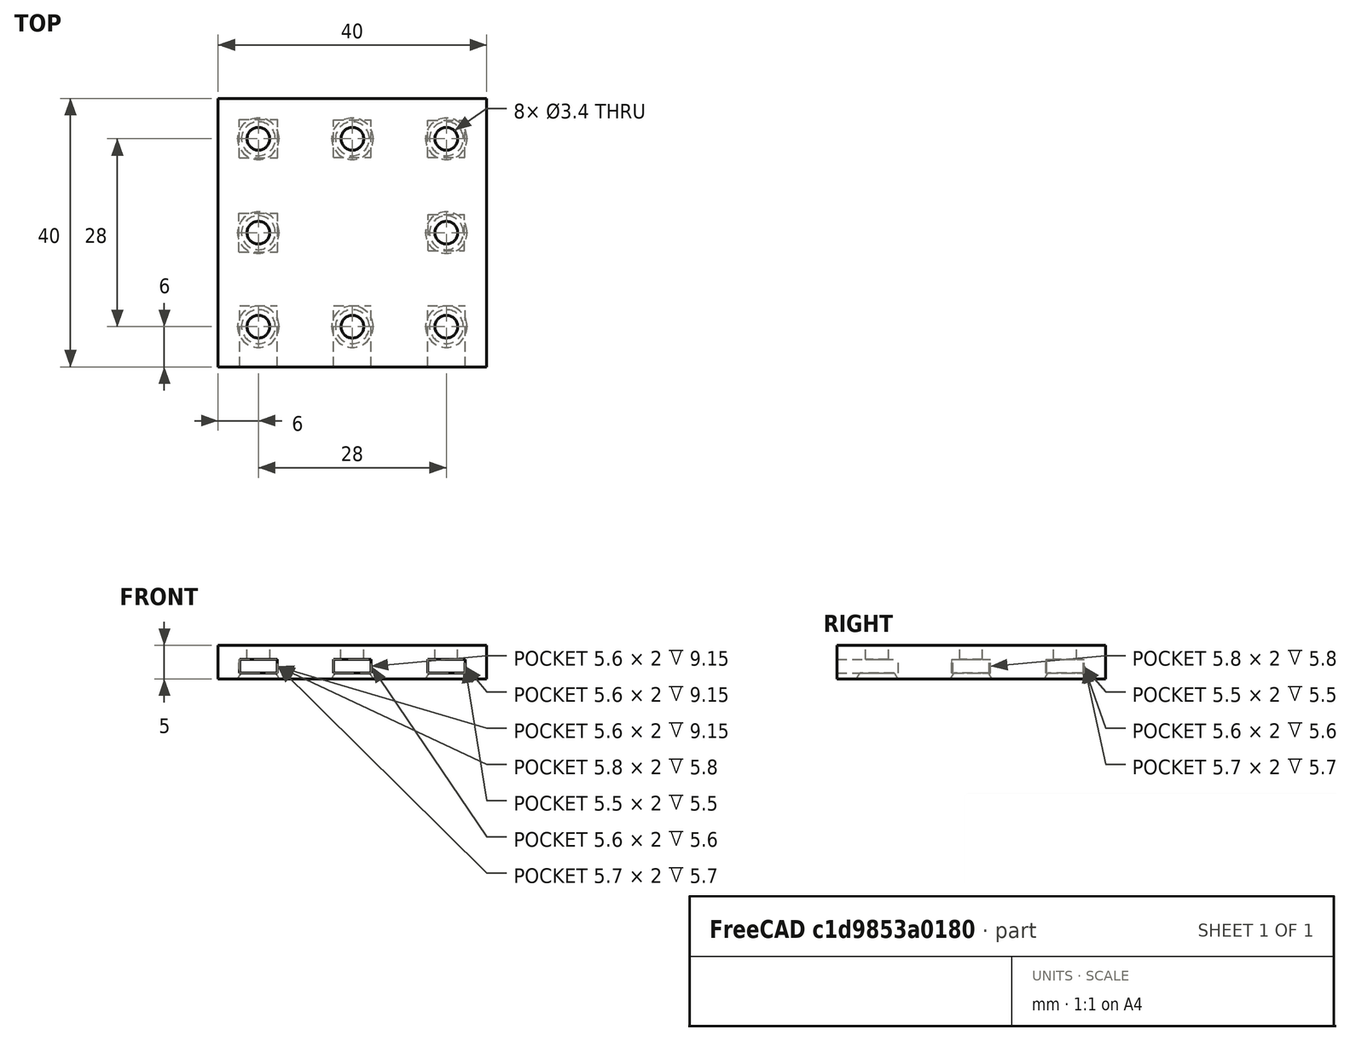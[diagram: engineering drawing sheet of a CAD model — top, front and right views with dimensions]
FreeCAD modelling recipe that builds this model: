
FCSTD DOCUMENT  (FreeCAD 0.17R13522 (Git))
Label: Face plates with imbedded nuts
License: All rights reserved
LicenseURL: http://en.wikipedia.org/wiki/All_rights_reserved
objects: Part::Box×9, Part::Sphere×8, Part::Cylinder×8, Part::MultiFuse×3, Part::Cut×3
note: 31 computed .brp shape members not serialized (recipe doc carries the construction recipe); baked Part::Feature solids carry a one-line shape summary decoded from their .brp

FEATURE [Part::Box] Box001  label="Cube001"
  AttacherType = Attacher::AttachEngine3D
  Height = 5
  Length = 40
  Placement = pos=(0,0,3.7) rot=(0,0,1;0rad)
  Width = 40
FEATURE [Part::Box] Box011  label="Square Nut Hole 008"
  AttacherType = Attacher::AttachEngine3D
  Height = 2
  Length = 5.6
  Placement = pos=(17.2,31.2,4.6) rot=(0,0,1;0rad)
  Width = 5.6
FEATURE [Part::Box] Box012  label="Square Nut Hole 009"
  AttacherType = Attacher::AttachEngine3D
  Height = 2
  Length = 5.6
  Placement = pos=(17.2,-0.85,4.6) rot=(0,0,1;0rad)
  Width = 10
FEATURE [Part::Box] Box013  label="Square Nut Hole 010"
  AttacherType = Attacher::AttachEngine3D
  Height = 2
  Length = 5.6
  Placement = pos=(31.2,-0.85,4.6) rot=(0,0,1;0rad)
  Width = 10
FEATURE [Part::Box] Box014  label="Square Nut Hole 011"
  AttacherType = Attacher::AttachEngine3D
  Height = 2
  Length = 5.4
  Placement = pos=(31.3,17.3,4.6) rot=(0,0,1;0rad)
  Width = 5.4
FEATURE [Part::Box] Box015  label="Square Nut Hole 012"
  AttacherType = Attacher::AttachEngine3D
  Height = 2
  Length = 5.7
  Placement = pos=(3.15,31.15,4.6) rot=(0,0,1;0rad)
  Width = 5.7
FEATURE [Part::Box] Box016  label="Square Nut Hole 013"
  AttacherType = Attacher::AttachEngine3D
  Height = 2
  Length = 5.5
  Placement = pos=(31.25,31.25,4.6) rot=(0,0,1;0rad)
  Width = 5.5
FEATURE [Part::Box] Box017  label="Square Nut Hole 014"
  AttacherType = Attacher::AttachEngine3D
  Height = 2
  Length = 5.8
  Placement = pos=(3.1,17.1,4.6) rot=(0,0,1;0rad)
  Width = 5.8
FEATURE [Part::Box] Box018  label="Square Nut Hole 015"
  AttacherType = Attacher::AttachEngine3D
  Height = 2
  Length = 5.6
  Placement = pos=(3.2,-0.85,4.6) rot=(0,0,1;0rad)
  Width = 10
FEATURE [Part::Sphere] Sphere006  label="Nut Clearence1"
  Angle1 = -90
  Angle2 = 90
  Angle3 = 360
  AttacherType = Attacher::AttachEngine3D
  Placement = pos=(6,6,2.4) rot=(0,0,1;0rad)
  Radius = 3.35
FEATURE [Part::Sphere] Sphere007
  Angle1 = -90
  Angle2 = 90
  Angle3 = 360
  AttacherType = Attacher::AttachEngine3D
  Placement = pos=(34,20,2.4) rot=(0,0,1;0rad)
  Radius = 3.35
FEATURE [Part::Sphere] Sphere008
  Angle1 = -90
  Angle2 = 90
  Angle3 = 360
  AttacherType = Attacher::AttachEngine3D
  Placement = pos=(6,34,2.4) rot=(0,0,1;0rad)
  Radius = 3.35
FEATURE [Part::Sphere] Sphere001
  Angle1 = -90
  Angle2 = 90
  Angle3 = 360
  AttacherType = Attacher::AttachEngine3D
  Placement = pos=(34,6,2.4) rot=(0,0,1;0rad)
  Radius = 3.35
FEATURE [Part::Sphere] Sphere009
  Angle1 = -90
  Angle2 = 90
  Angle3 = 360
  AttacherType = Attacher::AttachEngine3D
  Placement = pos=(20,6,2.4) rot=(0,0,1;0rad)
  Radius = 3.35
FEATURE [Part::Sphere] Sphere010
  Angle1 = -90
  Angle2 = 90
  Angle3 = 360
  AttacherType = Attacher::AttachEngine3D
  Placement = pos=(20,34,2.4) rot=(0,0,1;0rad)
  Radius = 3.35
FEATURE [Part::Sphere] Sphere004
  Angle1 = -90
  Angle2 = 90
  Angle3 = 360
  AttacherType = Attacher::AttachEngine3D
  Placement = pos=(6,20,2.4) rot=(0,0,1;0rad)
  Radius = 3.35
FEATURE [Part::Sphere] Sphere002
  Angle1 = -90
  Angle2 = 90
  Angle3 = 360
  AttacherType = Attacher::AttachEngine3D
  Placement = pos=(34,34,2.4) rot=(0,0,1;0rad)
  Radius = 3.35
FEATURE [Part::Cylinder] Cylinder
  Angle = 360
  AttacherType = Attacher::AttachEngine3D
  Height = 10
  Placement = pos=(6,6,0) rot=(0,0,1;0rad)
  Radius = 1.7
FEATURE [Part::Cylinder] Cylinder002
  Angle = 360
  AttacherType = Attacher::AttachEngine3D
  Height = 10
  Placement = pos=(34,6,0) rot=(0,0,1;0rad)
  Radius = 1.7
FEATURE [Part::Cylinder] Cylinder001
  Angle = 360
  AttacherType = Attacher::AttachEngine3D
  Height = 10
  Placement = pos=(20,6,0) rot=(0,0,1;0rad)
  Radius = 1.7
FEATURE [Part::Cylinder] Cylinder003
  Angle = 360
  AttacherType = Attacher::AttachEngine3D
  Height = 10
  Placement = pos=(34,34,0) rot=(0,0,1;0rad)
  Radius = 1.7
FEATURE [Part::Cylinder] Cylinder004
  Angle = 360
  AttacherType = Attacher::AttachEngine3D
  Height = 10
  Placement = pos=(20,34,0) rot=(0,0,1;0rad)
  Radius = 1.7
FEATURE [Part::Cylinder] Cylinder005
  Angle = 360
  AttacherType = Attacher::AttachEngine3D
  Height = 10
  Placement = pos=(6,34,0) rot=(0,0,1;0rad)
  Radius = 1.7
FEATURE [Part::Cylinder] Cylinder006
  Angle = 360
  AttacherType = Attacher::AttachEngine3D
  Height = 10
  Placement = pos=(6,20,0) rot=(0,0,1;0rad)
  Radius = 1.7
FEATURE [Part::Cylinder] Cylinder007
  Angle = 360
  AttacherType = Attacher::AttachEngine3D
  Height = 10
  Placement = pos=(34,20,0) rot=(0,0,1;0rad)
  Radius = 1.7
FEATURE [Part::MultiFuse] Fusion002
  Shapes = -> [Cylinder,Cylinder004,Cylinder007,Cylinder005,Cylinder006,Cylinder001,Cylinder002,Cylinder003]
FEATURE [Part::MultiFuse] Fusion003
  Shapes = -> [Sphere007,Sphere008,Sphere006,Sphere009,Sphere001,Sphere010,Sphere004,Sphere002]
FEATURE [Part::MultiFuse] Fusion
  Shapes = -> [Box013,Box017,Box014,Box015,Box016,Box018,Box011,Box012]
FEATURE [Part::Cut] Cut
  Base = -> Box001
  Tool = -> Fusion
FEATURE [Part::Cut] Cut001
  Base = -> Cut
  Tool = -> Fusion003
FEATURE [Part::Cut] Cut002
  Base = -> Cut001
  Tool = -> Fusion002
